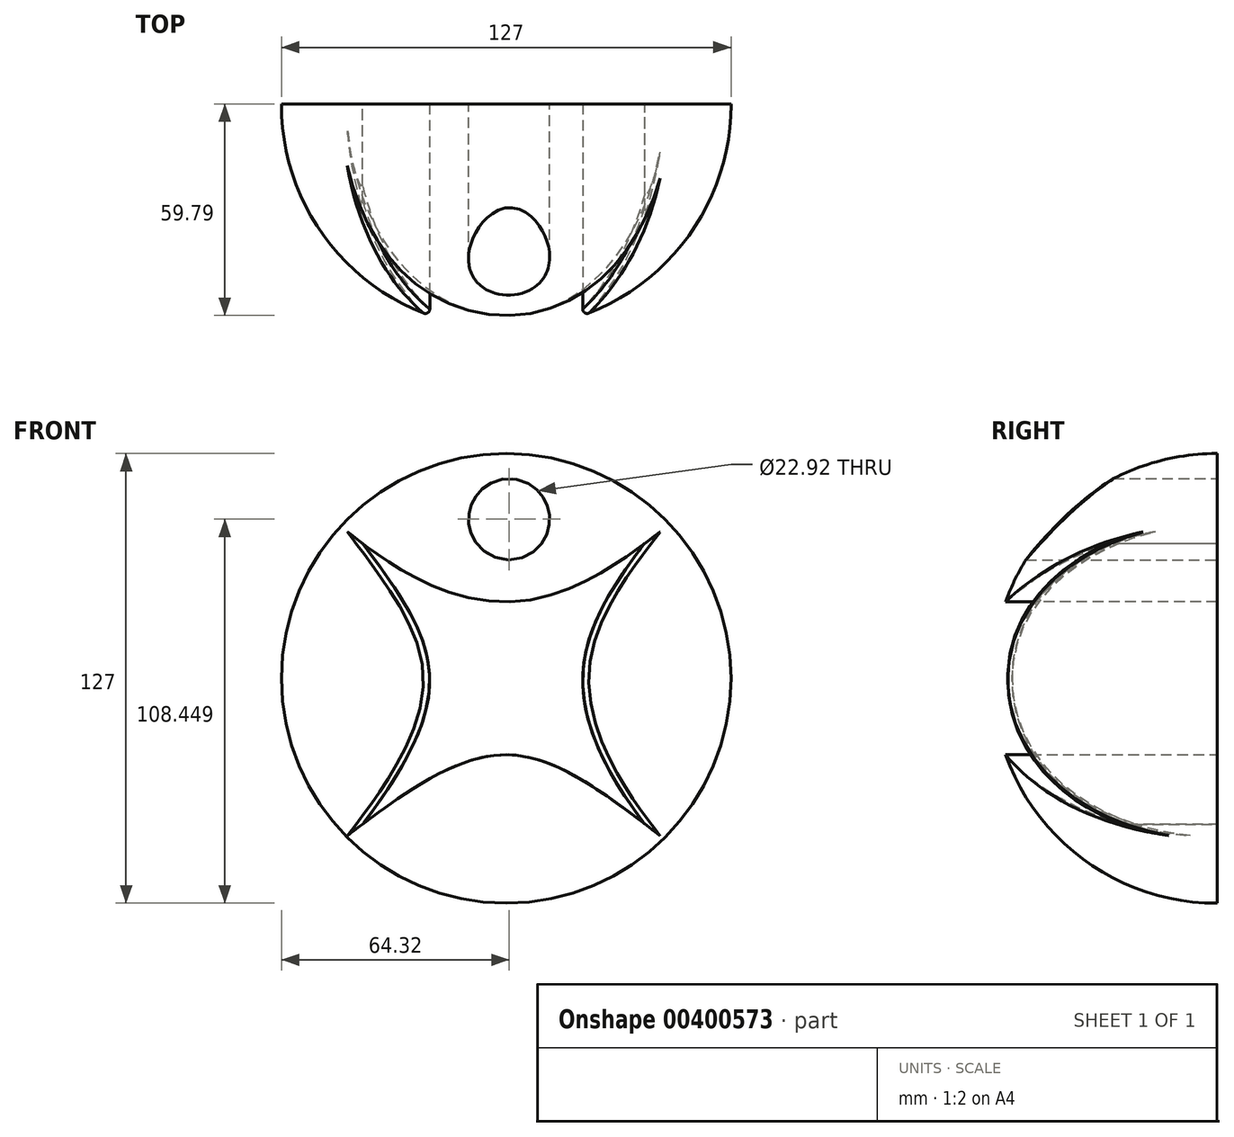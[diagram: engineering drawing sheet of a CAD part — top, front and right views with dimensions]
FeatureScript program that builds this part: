
annotation { "Feature Type Name" : "Feature", "Feature Type Description" : "" }
export const myFeature = defineFeature(function(context is Context, id is Id, definition is map)
    precondition{}
    {
        {
            var Q0;
            Q0=qCreatedBy(makeId("Front.planeOp"),FACE);
            var sketch = newSketch(context, id + "F0", { "sketchPlane" : qUnion([Q0])});
            skCircle(sketch, "E0", {"center": v(0, 0) * mm, "radius": 63.5 * mm});
            skPoint(sketch, "E1", {"position": v(-21.59, 0) * mm});
            skPoint(sketch, "E2", {"position": v(21.59, 0) * mm});
            skPoint(sketch, "E3", {"position": v(0, 21.59) * mm});
            skPoint(sketch, "E4", {"position": v(0, -21.59) * mm});
            skPoint(sketch, "E5", {"position": v(39.1, -41.1) * mm});
            skPoint(sketch, "E6", {"position": v(-40.54, 38.1) * mm});
            skPoint(sketch, "E7", {"position": v(-40.54, -41.17) * mm});
            skPoint(sketch, "E8", {"position": v(39.1, 38.1) * mm});
            skFitSpline(sketch, "E9", {"points": [v(-40.54, 38.1) * mm, v(0, 21.59) * mm, v(39.1, 38.1) * mm], "startDerivative": vector(87.27, -66.16) * mm, "endDerivative": vector(88, 66.08) * mm});
            skFitSpline(sketch, "E10", {"points": [v(-40.54, 38.1) * mm, v(-21.59, 0) * mm, v(-40.54, -41.17) * mm], "startDerivative": vector(66.06, -87.25) * mm, "endDerivative": vector(-66.09, -86.97) * mm});
            skFitSpline(sketch, "E11", {"points": [v(-40.54, -41.17) * mm, v(0, -21.59) * mm, v(39.1, -41.1) * mm], "startDerivative": vector(87.43, 66) * mm, "endDerivative": vector(87.84, -66.96) * mm});
            skFitSpline(sketch, "E12", {"points": [v(39.1, 38.1) * mm, v(21.59, 0) * mm, v(39.1, -41.1) * mm], "startDerivative": vector(-67.34, -87.3) * mm, "endDerivative": vector(67.26, -88) * mm});
            skSolve(sketch);
        }
        {
            var Q0;
            Q0=makeQuery(id+"F0.imprint","IMPRINT",FACE,{"disambiguationData":[TD([[makeQuery(id+"F0.imprint","IMPRINT",EDGE,{"derivedFrom":sQuery(id+"F0.wireOp",EDGE,"E0")}),1.0]])]});
            extrude(context, id + "F1", {"entities" : qUnion([Q0]), "depth" : 63.5 * mm});
        }
        {
            var Q0;
            Q0=makeQuery(id+"F1.opExtrude","CAP_EDGE",EDGE,{"disambiguationData":[OSD([sQuery(id+"F0.wireOp",EDGE,"E0")])],"isStart":false});
            fillet(context, id + "F2", {"entities" : qUnion([Q0]), "radius" : 63.25 * mm, "tangentPropagation" : true, "allowEdgeOverflow" : false});
        }
        {
            var Q0;
            Q0=makeQuery(id+"F2.opFillet","BLEND_EDGE",EDGE,{"disambiguationData":[OD(1.0)],"blendedFrom":[makeQuery(id+"F1.opExtrude","CAP_EDGE",EDGE,{"disambiguationData":[OSD([sQuery(id+"F0.wireOp",EDGE,"E0")])],"isStart":false}),makeQuery(id+"F1.opExtrude","SWEPT_FACE",FACE,{"disambiguationData":[OSD([sQuery(id+"F0.wireOp",EDGE,"E12")])]})],"blendedInto":[makeQuery(id+"F1.opExtrude","SWEPT_FACE",FACE,{"disambiguationData":[OSD([sQuery(id+"F0.wireOp",EDGE,"E12")])]})]});
            fillet(context, id + "F3", {"entities" : qUnion([Q0]), "radius" : 1.27 * mm, "tangentPropagation" : true, "allowEdgeOverflow" : false});
        }
        {
            var Q0;
            Q0=makeQuery(id+"F2.opFillet","BLEND_EDGE",EDGE,{"blendedFrom":[makeQuery(id+"F1.opExtrude","CAP_EDGE",EDGE,{"disambiguationData":[OSD([sQuery(id+"F0.wireOp",EDGE,"E0")])],"isStart":false}),makeQuery(id+"F1.opExtrude","SWEPT_FACE",FACE,{"disambiguationData":[OSD([sQuery(id+"F0.wireOp",EDGE,"E10")])]})],"blendedInto":[makeQuery(id+"F1.opExtrude","SWEPT_FACE",FACE,{"disambiguationData":[OSD([sQuery(id+"F0.wireOp",EDGE,"E10")])]})]});
            fillet(context, id + "F4", {"entities" : qUnion([Q0]), "radius" : 1.27 * mm, "tangentPropagation" : true, "allowEdgeOverflow" : false});
        }
        {
            var Q0;
            Q0=makeQuery(id+"F0.imprint","IMPRINT",FACE,{"disambiguationData":[TD([[makeQuery(id+"F0.imprint","IMPRINT",EDGE,{"derivedFrom":sQuery(id+"F0.wireOp",EDGE,"E0")}),1.0]])]});
            var sketch = newSketch(context, id + "F5", { "sketchPlane" : qUnion([Q0])});
            skCircle(sketch, "E13", {"center": v(0.82, 44.95) * mm, "radius": 11.46 * mm});
            skPoint(sketch, "E13.first.point", {"position": v(0, 56.38) * mm});
            skPoint(sketch, "E13.second.point", {"position": v(0, 33.52) * mm});
            skPoint(sketch, "E13.third.point", {"position": v(12.2, 43.62) * mm});
            skSolve(sketch);
        }
        {
            var Q0;
            Q0=makeQuery(id+"F5.imprint","IMPRINT",FACE,{"disambiguationData":[TD([[makeQuery(id+"F5.imprint","IMPRINT",EDGE,{"derivedFrom":sQuery(id+"F5.wireOp",EDGE,"E13")}),1.0]])]});
            extrude(context, id + "F6", {"entities" : qUnion([Q0]), "operationType" : NewBodyOperationType.REMOVE, "depth" : 76.2 * mm});
        }
    });
